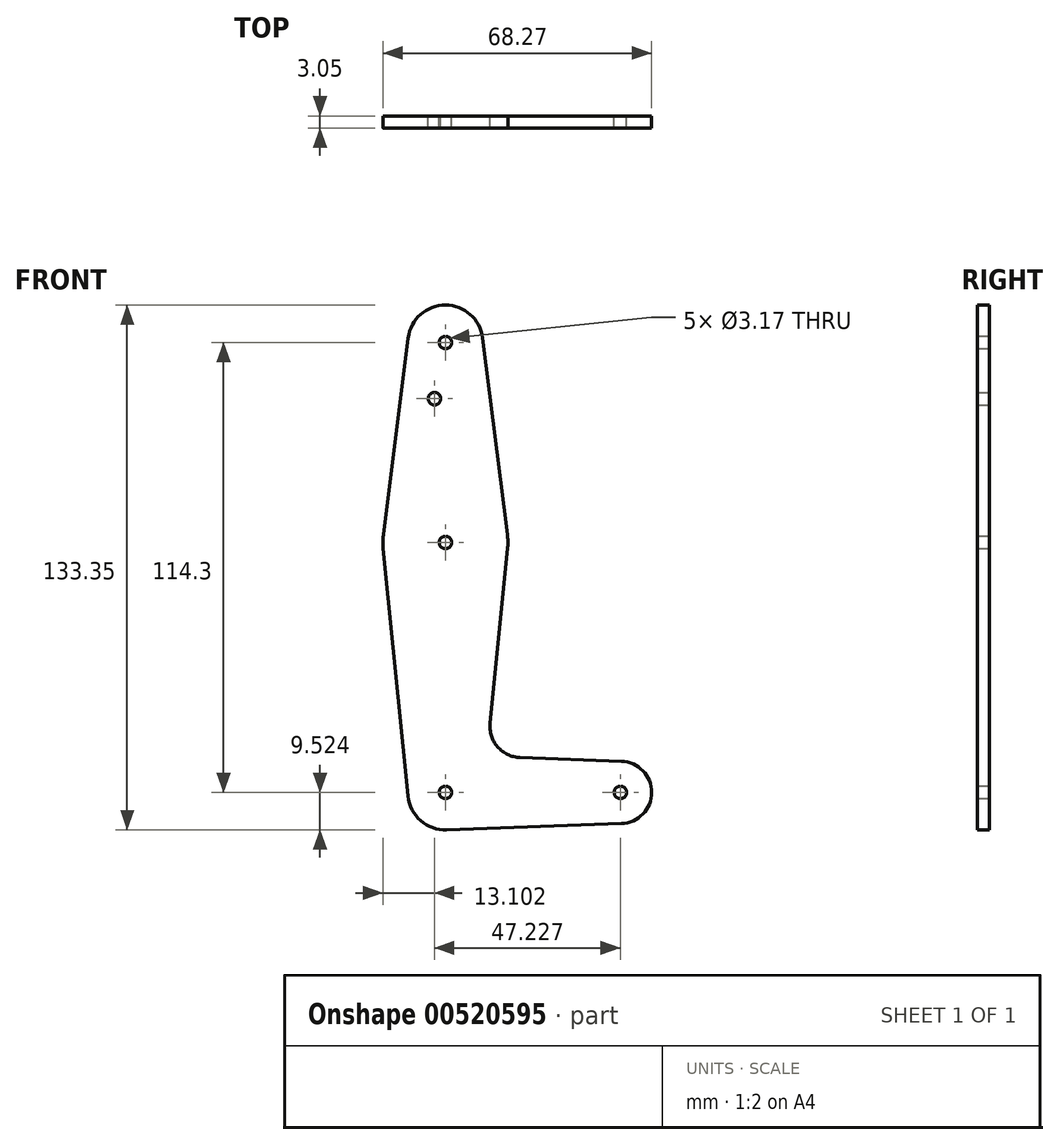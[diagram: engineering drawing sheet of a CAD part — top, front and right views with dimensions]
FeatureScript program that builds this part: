
annotation { "Feature Type Name" : "Feature", "Feature Type Description" : "" }
export const myFeature = defineFeature(function(context is Context, id is Id, definition is map)
    precondition{}
    {
        {
            var Q0;
            Q0=qCreatedBy(makeId("Front.planeOp"),FACE);
            var sketch = newSketch(context, id + "F0", { "sketchPlane" : qUnion([Q0])});
            skLineSegment(sketch, "E0", {"start": v(-23, 43.43) * mm, "end": v(-23, -70.87) * mm, "construction": true});
            skLineSegment(sketch, "E1", {"start": v(-23, -70.87) * mm, "end": v(21.46, -70.87) * mm, "construction": true});
            skCircle(sketch, "E2", {"center": v(-23, 43.43) * mm, "radius": 9.53 * mm});
            skCircle(sketch, "E3", {"center": v(-23, -70.87) * mm, "radius": 9.53 * mm});
            skCircle(sketch, "E4", {"center": v(21.46, -70.87) * mm, "radius": 7.94 * mm});
            skCircle(sketch, "E5", {"center": v(-23, -7.37) * mm, "radius": 15.88 * mm});
            skLineSegment(sketch, "E6", {"start": v(-32.44, 44.62) * mm, "end": v(-38.74, -5.38) * mm});
            skLineSegment(sketch, "E7", {"start": v(-38.79, -8.95) * mm, "end": v(-32.47, -71.82) * mm});
            skLineSegment(sketch, "E8", {"start": v(-22.65, -80.38) * mm, "end": v(21.74, -78.8) * mm});
            skLineSegment(sketch, "E9", {"start": v(21.74, -62.93) * mm, "end": v(-4.02, -62.01) * mm});
            skLineSegment(sketch, "E10", {"start": v(-7.2, -8.95) * mm, "end": v(-11.65, -53.27) * mm});
            skLineSegment(sketch, "E11", {"start": v(-7.24, -5.38) * mm, "end": v(-13.54, 44.62) * mm});
            skCircle(sketch, "E12", {"center": v(-23, 43.43) * mm, "radius": 1.59 * mm});
            skCircle(sketch, "E13", {"center": v(-25.77, 29.16) * mm, "radius": 1.59 * mm});
            skCircle(sketch, "E14", {"center": v(-23, -7.37) * mm, "radius": 1.59 * mm});
            skCircle(sketch, "E15", {"center": v(-23, -70.87) * mm, "radius": 1.59 * mm});
            skCircle(sketch, "E16", {"center": v(21.46, -70.87) * mm, "radius": 1.59 * mm});
            skArc(sketch, "E17.filletArc", {"start": v(-11.65, -53.27) * mm, "mid": v(-9.73, -59.3) * mm, "end": v(-4.02, -62.01) * mm});
            skSolve(sketch);
        }
        {
            var Q0;
            Q0 = qSketchRegion(id + "F0", true);
            extrude(context, id + "F1", {"entities" : qUnion([Q0]), "depth" : 3.05 * mm, "offsetDistance" : 25.4 * mm});
        }
    });
